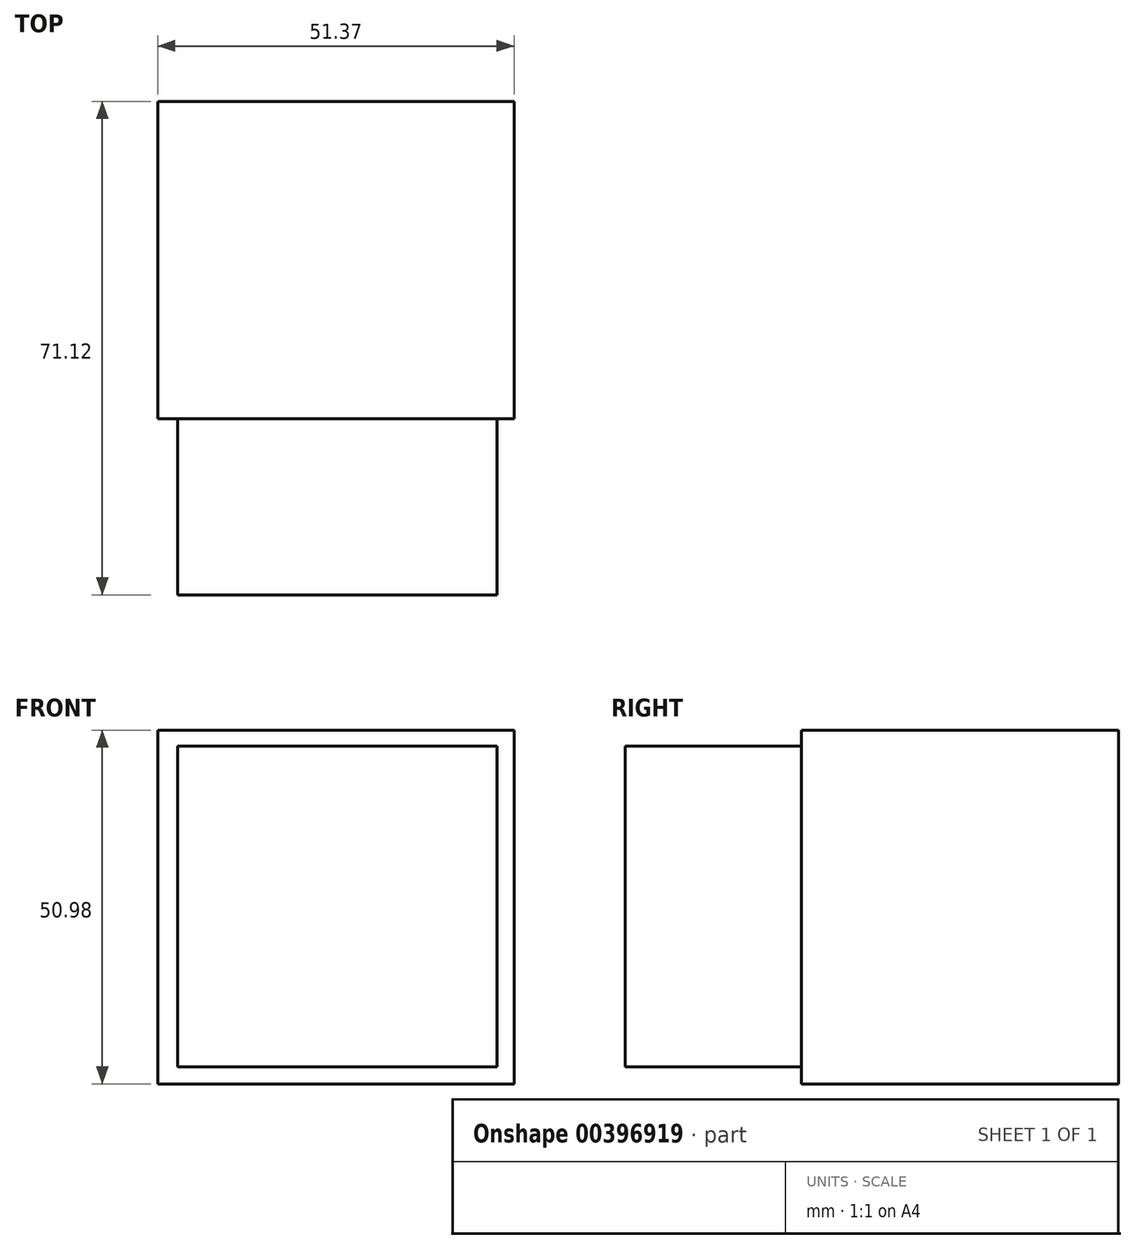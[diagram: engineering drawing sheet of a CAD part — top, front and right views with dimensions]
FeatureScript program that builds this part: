
annotation { "Feature Type Name" : "Feature", "Feature Type Description" : "" }
export const myFeature = defineFeature(function(context is Context, id is Id, definition is map)
    precondition{}
    {
        {
            var Q0;
            Q0=qCreatedBy(makeId("Front.planeOp"),FACE);
            var sketch = newSketch(context, id + "F0", { "sketchPlane" : qUnion([Q0])});
            skLineSegment(sketch, "E0.bottom", {"start": v(0, 0) * mm, "end": v(-51.37, 0) * mm});
            skLineSegment(sketch, "E0.top", {"start": v(0, 50.98) * mm, "end": v(-51.37, 50.98) * mm});
            skLineSegment(sketch, "E0.left", {"start": v(0, 0) * mm, "end": v(0, 50.98) * mm});
            skLineSegment(sketch, "E0.right", {"start": v(-51.37, 0) * mm, "end": v(-51.37, 50.98) * mm});
            skLineSegment(sketch, "E1.bottom", {"start": v(-24.06, -4.96) * mm, "end": v(-24.44, -4.96) * mm});
            skLineSegment(sketch, "E1.top", {"start": v(-24.06, -6.5) * mm, "end": v(-24.44, -6.5) * mm});
            skLineSegment(sketch, "E1.left", {"start": v(-24.06, -4.96) * mm, "end": v(-24.06, -6.5) * mm});
            skLineSegment(sketch, "E1.right", {"start": v(-24.44, -4.96) * mm, "end": v(-24.44, -6.5) * mm});
            skSolve(sketch);
        }
        {
            var Q0;
            Q0=makeQuery(id+"F0.imprint","IMPRINT",FACE,{"disambiguationData":[TD([[makeQuery(id+"F0.imprint","IMPRINT",EDGE,{"derivedFrom":sQuery(id+"F0.wireOp",EDGE,"E0.bottom")}),-1.0]])]});
            extrude(context, id + "F1", {"entities" : qUnion([Q0]), "depth" : 45.72 * mm});
        }
        {
            var Q0;
            Q0=makeQuery(id+"F1.opExtrude","CAP_FACE",FACE,{"disambiguationData":[OSD([sQuery(id+"F0.wireOp",EDGE,"E0.bottom"),sQuery(id+"F0.wireOp",EDGE,"E0.top"),sQuery(id+"F0.wireOp",EDGE,"E0.left"),sQuery(id+"F0.wireOp",EDGE,"E0.right")])],"isStart":false});
            var sketch = newSketch(context, id + "F2", { "sketchPlane" : qUnion([Q0])});
            skLineSegment(sketch, "E2.bottom", {"start": v(-2.48, 2.48) * mm, "end": v(-48.5, 2.48) * mm});
            skLineSegment(sketch, "E2.top", {"start": v(-2.48, 48.7) * mm, "end": v(-48.5, 48.7) * mm});
            skLineSegment(sketch, "E2.left", {"start": v(-2.48, 2.48) * mm, "end": v(-2.48, 48.7) * mm});
            skLineSegment(sketch, "E2.right", {"start": v(-48.5, 2.48) * mm, "end": v(-48.5, 48.7) * mm});
            skSolve(sketch);
        }
        {
            var Q0;
            Q0=makeQuery(id+"F2.imprint","IMPRINT",FACE,{"disambiguationData":[TD([[makeQuery(id+"F2.imprint","IMPRINT",EDGE,{"derivedFrom":sQuery(id+"F2.wireOp",EDGE,"E2.bottom")}),-1.0]])]});
            extrude(context, id + "F3", {"entities" : qUnion([Q0]), "operationType" : NewBodyOperationType.ADD, "depth" : 25.4 * mm});
        }
    });
